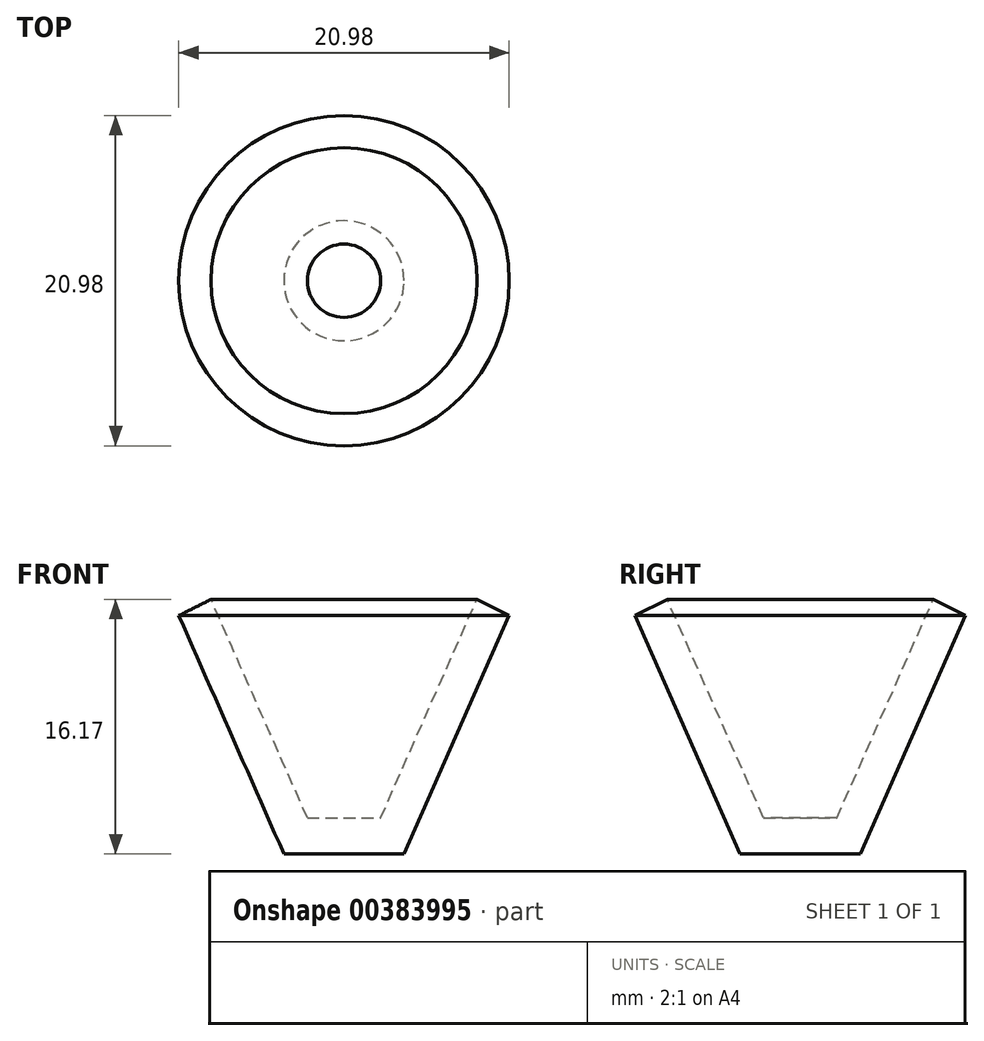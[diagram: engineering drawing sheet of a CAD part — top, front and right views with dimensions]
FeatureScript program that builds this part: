
annotation { "Feature Type Name" : "Feature", "Feature Type Description" : "" }
export const myFeature = defineFeature(function(context is Context, id is Id, definition is map)
    precondition{}
    {
        {
            var Q0;
            Q0=qCreatedBy(makeId("Front.planeOp"),FACE);
            var sketch = newSketch(context, id + "F0", { "sketchPlane" : qUnion([Q0])});
            skLineSegment(sketch, "E0", {"start": v(0, 0) * mm, "end": v(0, 2.29) * mm});
            skLineSegment(sketch, "E1", {"start": v(0, 2.29) * mm, "end": v(2.32, 2.29) * mm});
            skLineSegment(sketch, "E2", {"start": v(2.32, 2.29) * mm, "end": v(8.45, 16.17) * mm});
            skLineSegment(sketch, "E3.0", {"start": v(3.81, 0) * mm, "end": v(10.5, 15.14) * mm});
            skLineSegment(sketch, "E3.1", {"start": v(0, 0) * mm, "end": v(3.81, 0) * mm});
            skLineSegment(sketch, "E4", {"start": v(8.45, 16.17) * mm, "end": v(10.5, 15.14) * mm});
            skLineSegment(sketch, "E5", {"start": v(0, 0) * mm, "end": v(0, 26.2) * mm});
            skSolve(sketch);
        }
        {
            var Q0;
            Q0=makeQuery(id+"F0.imprint","IMPRINT",FACE,{"disambiguationData":[TD([[makeQuery(id+"F0.imprint","IMPRINT",EDGE,{"derivedFrom":sQuery(id+"F0.wireOp",EDGE,"E0")}),-1.0]])]});
            var Q1;
            Q1=sQuery(id+"F0.wireOp",EDGE,"E5");
            revolve(context, id + "F1", {"surfaceOperationType" : NewSurfaceOperationType.NEW, "entities" : qUnion([Q0]), "axis" : qUnion([Q1]), "revolveType" : RevolveType.FULL});
        }
    });
